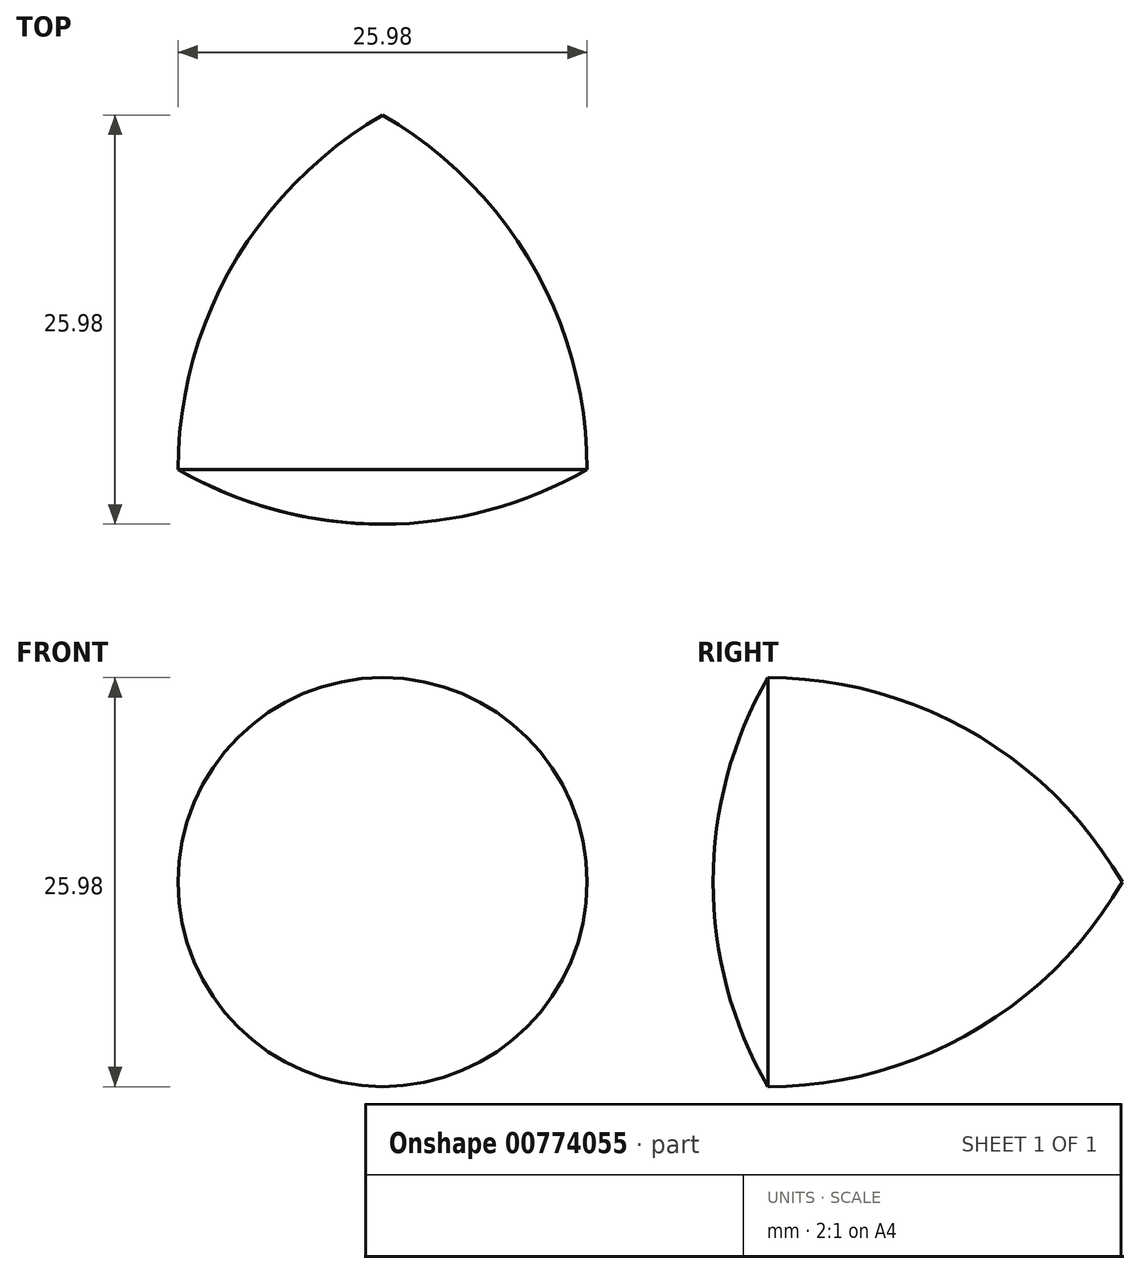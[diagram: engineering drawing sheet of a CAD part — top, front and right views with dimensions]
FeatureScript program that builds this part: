
annotation { "Feature Type Name" : "Feature", "Feature Type Description" : "" }
export const myFeature = defineFeature(function(context is Context, id is Id, definition is map)
    precondition{}
    {
        {
            var Q0;
            Q0=qCreatedBy(makeId("Top.planeOp"),FACE);
            var sketch = newSketch(context, id + "F0", { "sketchPlane" : qUnion([Q0])});
            skCircle(sketch, "E0.cCircle", {"center": v(0, 0) * mm, "radius": 15 * mm, "construction": true});
            skLineSegment(sketch, "E0.0", {"start": v(0, 15) * mm, "end": v(13, -7.5) * mm});
            skLineSegment(sketch, "E0.1", {"start": v(13, -7.5) * mm, "end": v(-13, -7.5) * mm});
            skLineSegment(sketch, "E0.2", {"start": v(-13, -7.5) * mm, "end": v(0, 15) * mm});
            skCircle(sketch, "E1", {"center": v(0, 15) * mm, "radius": 25.98 * mm});
            skCircle(sketch, "E2", {"center": v(-13, -7.5) * mm, "radius": 25.98 * mm});
            skCircle(sketch, "E3", {"center": v(13, -7.5) * mm, "radius": 25.98 * mm});
            skLineSegment(sketch, "E4", {"start": v(0, 15) * mm, "end": v(0, -10.98) * mm});
            skPoint(sketch, "E4.endSnap0", {"position": v(0, -7.5) * mm});
            skSolve(sketch);
        }
        {
            var Q0;
            {var subQ0=sQuery(id+"F0.wireOp",EDGE,"E0.2");Q0=makeQuery(id+"F0.imprint","IMPRINT",FACE,{"disambiguationData":[TD([[makeQuery(id+"F0.imprint","IMPRINT",EDGE,{"derivedFrom":subQ0}),1.0]])]});}
            var Q1;
            {var subQ1=sQuery(id+"F0.wireOp",EDGE,"E0.2");Q1=makeQuery(id+"F0.imprint","IMPRINT",FACE,{"disambiguationData":[TD([[makeQuery(id+"F0.imprint","IMPRINT",EDGE,{"derivedFrom":subQ1}),-1.0]])]});}
            var Q2;
            {var subQ0=sQuery(id+"F0.wireOp",EDGE,"E1");var subQ3=sQuery(id+"F0.wireOp",EDGE,"E4");var subQ5=makeQuery(id+"F0.imprint","INTERSECT",VERTEX,{"derivedFrom":[subQ0,subQ3]});Q2=makeQuery(id+"F0.imprint","IMPRINT",FACE,{"disambiguationData":[TD([[makeQuery(id+"F0.imprint","IMPRINT",EDGE,{"disambiguationData":[TD([[subQ5,1.0]])],"derivedFrom":subQ3}),-1.0]])]});}
            var Q3;
            Q3=sQuery(id+"F0.wireOp",EDGE,"E4");
            revolve(context, id + "F1", {"surfaceOperationType" : NewSurfaceOperationType.NEW, "entities" : qUnion([Q0, Q1, Q2]), "axis" : qUnion([Q3]), "revolveType" : RevolveType.FULL});
        }
    });
